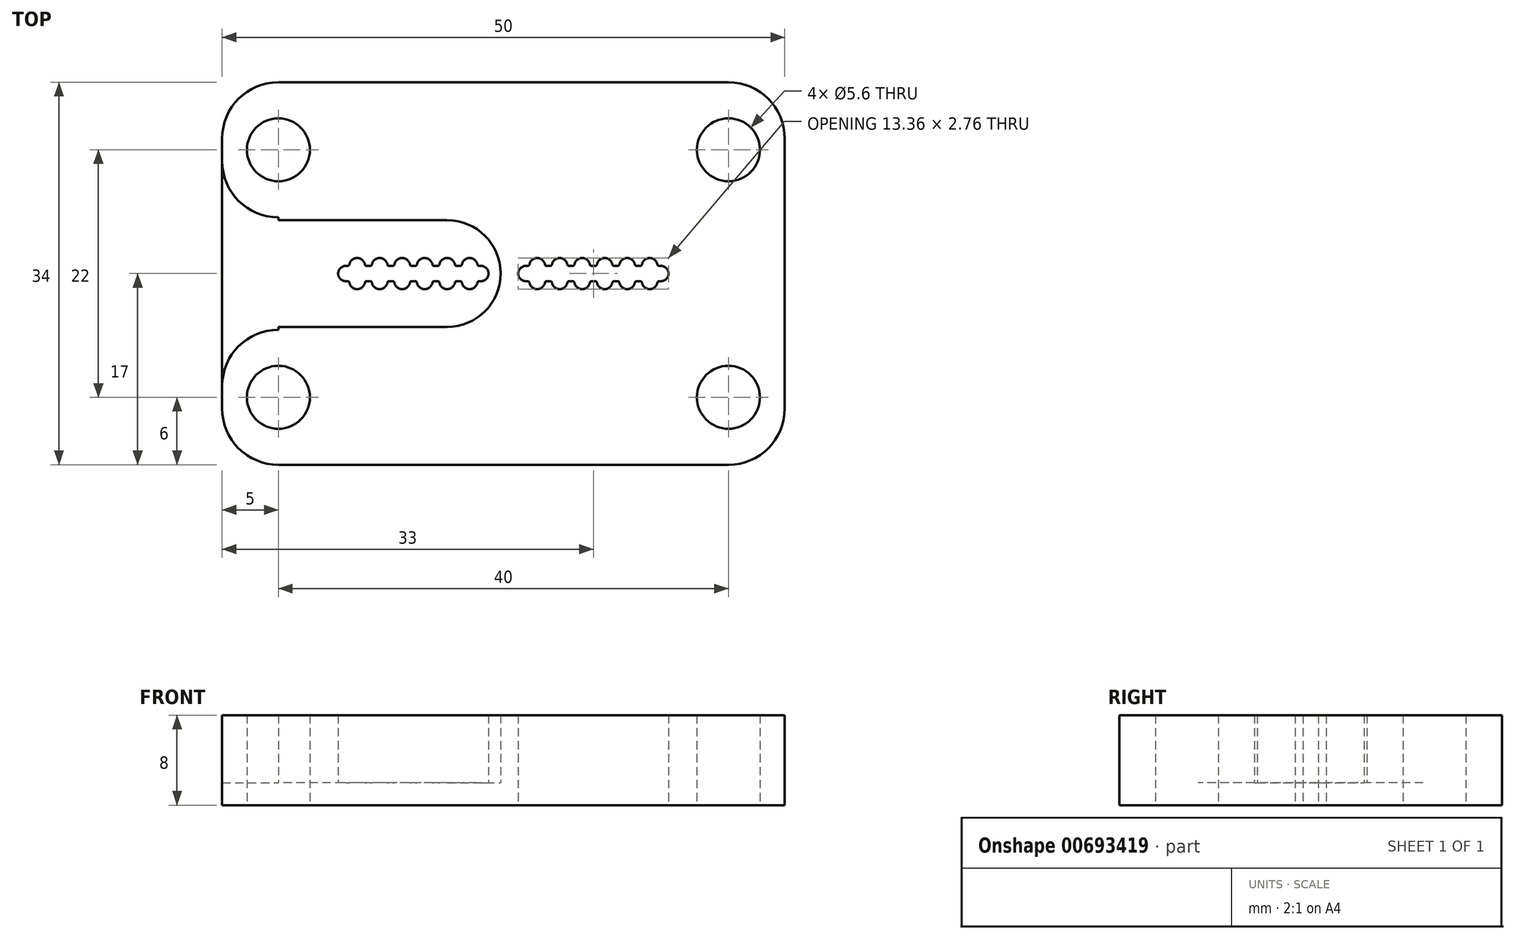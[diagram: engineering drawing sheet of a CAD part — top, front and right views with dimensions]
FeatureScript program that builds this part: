
annotation { "Feature Type Name" : "Feature", "Feature Type Description" : "" }
export const myFeature = defineFeature(function(context is Context, id is Id, definition is map)
    precondition{}
    {
        {
            var Q0;
            Q0=qCreatedBy(makeId("Top.planeOp"),FACE);
            var sketch = newSketch(context, id + "F0", { "sketchPlane" : qUnion([Q0])});
            skLineSegment(sketch, "E0.bottom", {"start": v(-25, 17) * mm, "end": v(25, 17) * mm, "construction": true});
            skLineSegment(sketch, "E0.top", {"start": v(-25, -17) * mm, "end": v(25, -17) * mm, "construction": true});
            skLineSegment(sketch, "E0.left", {"start": v(-25, -10) * mm, "end": v(-25, -12) * mm, "construction": true});
            skLineSegment(sketch, "E0.right", {"start": v(25, 17) * mm, "end": v(25, -17) * mm, "construction": true});
            skPoint(sketch, "E0.middle", {"position": v(0, 0) * mm});
            skLineSegment(sketch, "E1", {"start": v(25, 0) * mm, "end": v(-5, 0) * mm, "construction": true});
            skLineSegment(sketch, "E2", {"start": v(-4, 0) * mm, "end": v(-2, 0) * mm});
            skLineSegment(sketch, "E3", {"start": v(-2, 0.68) * mm, "end": v(-2.16, 0.68) * mm});
            skArc(sketch, "E4", {"start": v(-2.31, 0.8) * mm, "mid": v(-3, 1.38) * mm, "end": v(-3.69, 0.8) * mm});
            skArc(sketch, "E5.filletArc", {"start": v(-2.31, 0.8) * mm, "mid": v(-2.26, 0.71) * mm, "end": v(-2.16, 0.68) * mm});
            skLineSegment(sketch, "E6", {"start": v(-4, 0.68) * mm, "end": v(-3.84, 0.68) * mm});
            skPoint(sketch, "E7.visualSharp", {"position": v(-3.7, 0.68) * mm});
            skArc(sketch, "E7.filletArc", {"start": v(-3.84, 0.68) * mm, "mid": v(-3.74, 0.71) * mm, "end": v(-3.69, 0.8) * mm});
            skLineSegment(sketch, "E8", {"start": v(0, -17) * mm, "end": v(0, 17) * mm, "construction": true});
            skLineSegment(sketch, "E9.1.0.0", {"start": v(-6, 0.68) * mm, "end": v(-5.84, 0.68) * mm});
            skArc(sketch, "E9.1.0.1", {"start": v(-4.31, 0.8) * mm, "mid": v(-5, 1.38) * mm, "end": v(-5.69, 0.8) * mm});
            skArc(sketch, "E9.1.0.2", {"start": v(-5.84, 0.68) * mm, "mid": v(-5.74, 0.71) * mm, "end": v(-5.69, 0.8) * mm});
            skArc(sketch, "E9.1.0.3", {"start": v(-4.31, 0.8) * mm, "mid": v(-4.26, 0.71) * mm, "end": v(-4.16, 0.68) * mm});
            skLineSegment(sketch, "E9.1.0.4", {"start": v(-4, 0.68) * mm, "end": v(-4.16, 0.68) * mm});
            skLineSegment(sketch, "E9.2.0.0", {"start": v(-8, 0.68) * mm, "end": v(-7.84, 0.68) * mm});
            skArc(sketch, "E9.2.0.1", {"start": v(-6.31, 0.8) * mm, "mid": v(-7, 1.38) * mm, "end": v(-7.69, 0.8) * mm});
            skArc(sketch, "E9.2.0.2", {"start": v(-7.84, 0.68) * mm, "mid": v(-7.74, 0.71) * mm, "end": v(-7.69, 0.8) * mm});
            skArc(sketch, "E9.2.0.3", {"start": v(-6.31, 0.8) * mm, "mid": v(-6.26, 0.71) * mm, "end": v(-6.16, 0.68) * mm});
            skLineSegment(sketch, "E9.2.0.4", {"start": v(-6, 0.68) * mm, "end": v(-6.16, 0.68) * mm});
            skLineSegment(sketch, "E9.3.0.0", {"start": v(-10, 0.68) * mm, "end": v(-9.84, 0.68) * mm});
            skArc(sketch, "E9.3.0.1", {"start": v(-8.31, 0.8) * mm, "mid": v(-9, 1.38) * mm, "end": v(-9.69, 0.8) * mm});
            skArc(sketch, "E9.3.0.2", {"start": v(-9.84, 0.68) * mm, "mid": v(-9.74, 0.71) * mm, "end": v(-9.69, 0.8) * mm});
            skArc(sketch, "E9.3.0.3", {"start": v(-8.31, 0.8) * mm, "mid": v(-8.26, 0.71) * mm, "end": v(-8.16, 0.68) * mm});
            skLineSegment(sketch, "E9.3.0.4", {"start": v(-8, 0.68) * mm, "end": v(-8.16, 0.68) * mm});
            skLineSegment(sketch, "E9.4.0.0", {"start": v(-12, 0.68) * mm, "end": v(-11.84, 0.68) * mm});
            skArc(sketch, "E9.4.0.1", {"start": v(-10.31, 0.8) * mm, "mid": v(-11, 1.38) * mm, "end": v(-11.69, 0.8) * mm});
            skArc(sketch, "E9.4.0.2", {"start": v(-11.84, 0.68) * mm, "mid": v(-11.74, 0.71) * mm, "end": v(-11.69, 0.8) * mm});
            skArc(sketch, "E9.4.0.3", {"start": v(-10.31, 0.8) * mm, "mid": v(-10.26, 0.71) * mm, "end": v(-10.16, 0.68) * mm});
            skLineSegment(sketch, "E9.4.0.4", {"start": v(-10, 0.68) * mm, "end": v(-10.16, 0.68) * mm});
            skLineSegment(sketch, "E9.5.0.0", {"start": v(-14, 0.68) * mm, "end": v(-13.84, 0.68) * mm});
            skArc(sketch, "E9.5.0.1", {"start": v(-12.31, 0.8) * mm, "mid": v(-13, 1.38) * mm, "end": v(-13.69, 0.8) * mm});
            skArc(sketch, "E9.5.0.2", {"start": v(-13.84, 0.68) * mm, "mid": v(-13.74, 0.71) * mm, "end": v(-13.69, 0.8) * mm});
            skArc(sketch, "E9.5.0.3", {"start": v(-12.31, 0.8) * mm, "mid": v(-12.26, 0.71) * mm, "end": v(-12.16, 0.68) * mm});
            skLineSegment(sketch, "E9.5.0.4", {"start": v(-12, 0.68) * mm, "end": v(-12.16, 0.68) * mm});
            skLineSegment(sketch, "E9.direction1", {"start": v(-4, 0.68) * mm, "end": v(-6, 0.68) * mm, "construction": true});
            skLineSegment(sketch, "E10", {"start": v(-14, 0.68) * mm, "end": v(-14, 0) * mm});
            skLineSegment(sketch, "E11", {"start": v(-5, 0) * mm, "end": v(-4, 0) * mm});
            skLineSegment(sketch, "E12.MirrorCS", {"start": v(-14, -0.68) * mm, "end": v(-13.84, -0.68) * mm});
            skArc(sketch, "E13.MirrorCS", {"start": v(-13.84, -0.68) * mm, "mid": v(-13.74, -0.71) * mm, "end": v(-13.69, -0.8) * mm});
            skArc(sketch, "E14.MirrorCS", {"start": v(-12.31, -0.8) * mm, "mid": v(-13, -1.38) * mm, "end": v(-13.69, -0.8) * mm});
            skArc(sketch, "E15.MirrorCS", {"start": v(-12.31, -0.8) * mm, "mid": v(-12.26, -0.71) * mm, "end": v(-12.16, -0.68) * mm});
            skLineSegment(sketch, "E16.MirrorCS", {"start": v(-12, -0.68) * mm, "end": v(-12.16, -0.68) * mm});
            skLineSegment(sketch, "E17.MirrorCS", {"start": v(-12, -0.68) * mm, "end": v(-11.84, -0.68) * mm});
            skArc(sketch, "E18.MirrorCS", {"start": v(-11.84, -0.68) * mm, "mid": v(-11.74, -0.71) * mm, "end": v(-11.69, -0.8) * mm});
            skArc(sketch, "E19.MirrorCS", {"start": v(-10.31, -0.8) * mm, "mid": v(-11, -1.38) * mm, "end": v(-11.69, -0.8) * mm});
            skArc(sketch, "E20.MirrorCS", {"start": v(-10.31, -0.8) * mm, "mid": v(-10.26, -0.71) * mm, "end": v(-10.16, -0.68) * mm});
            skLineSegment(sketch, "E21.MirrorCS", {"start": v(-10, -0.68) * mm, "end": v(-9.84, -0.68) * mm});
            skArc(sketch, "E22.MirrorCS", {"start": v(-9.84, -0.68) * mm, "mid": v(-9.74, -0.71) * mm, "end": v(-9.69, -0.8) * mm});
            skLineSegment(sketch, "E23.MirrorCS", {"start": v(-10, -0.68) * mm, "end": v(-10.16, -0.68) * mm});
            skArc(sketch, "E24.MirrorCS", {"start": v(-8.31, -0.8) * mm, "mid": v(-9, -1.38) * mm, "end": v(-9.69, -0.8) * mm});
            skArc(sketch, "E25.MirrorCS", {"start": v(-8.31, -0.8) * mm, "mid": v(-8.26, -0.71) * mm, "end": v(-8.16, -0.68) * mm});
            skArc(sketch, "E26.MirrorCS", {"start": v(-7.84, -0.68) * mm, "mid": v(-7.74, -0.71) * mm, "end": v(-7.69, -0.8) * mm});
            skLineSegment(sketch, "E27.MirrorCS", {"start": v(25, -17) * mm, "end": v(25, 17) * mm, "construction": true});
            skArc(sketch, "E28.MirrorCS", {"start": v(-6.31, -0.8) * mm, "mid": v(-7, -1.38) * mm, "end": v(-7.69, -0.8) * mm});
            skArc(sketch, "E29.MirrorCS", {"start": v(-6.31, -0.8) * mm, "mid": v(-6.26, -0.71) * mm, "end": v(-6.16, -0.68) * mm});
            skArc(sketch, "E30.MirrorCS", {"start": v(-5.84, -0.68) * mm, "mid": v(-5.74, -0.71) * mm, "end": v(-5.69, -0.8) * mm});
            skArc(sketch, "E31.MirrorCS", {"start": v(-4.31, -0.8) * mm, "mid": v(-5, -1.38) * mm, "end": v(-5.69, -0.8) * mm});
            skArc(sketch, "E32.MirrorCS", {"start": v(-4.31, -0.8) * mm, "mid": v(-4.26, -0.71) * mm, "end": v(-4.16, -0.68) * mm});
            skArc(sketch, "E33.MirrorCS", {"start": v(-3.84, -0.68) * mm, "mid": v(-3.74, -0.71) * mm, "end": v(-3.69, -0.8) * mm});
            skLineSegment(sketch, "E34.MirrorCS", {"start": v(-2, -0.68) * mm, "end": v(-2.16, -0.68) * mm});
            skArc(sketch, "E35.MirrorCS", {"start": v(-2.31, -0.8) * mm, "mid": v(-3, -1.38) * mm, "end": v(-3.69, -0.8) * mm});
            skArc(sketch, "E36.MirrorCS", {"start": v(-2.31, -0.8) * mm, "mid": v(-2.26, -0.71) * mm, "end": v(-2.16, -0.68) * mm});
            skLineSegment(sketch, "E37", {"start": v(-8.16, -0.68) * mm, "end": v(-7.84, -0.68) * mm});
            skLineSegment(sketch, "E38", {"start": v(-6.16, -0.68) * mm, "end": v(-5.84, -0.68) * mm});
            skLineSegment(sketch, "E39", {"start": v(-4.16, -0.68) * mm, "end": v(-3.84, -0.68) * mm});
            skArc(sketch, "E40", {"start": v(-2, -0.68) * mm, "mid": v(-1.32, 0) * mm, "end": v(-2, 0.68) * mm});
            skLineSegment(sketch, "E41.bottom", {"start": v(-20, -5) * mm, "end": v(-5, -5) * mm, "construction": true});
            skLineSegment(sketch, "E41.top", {"start": v(-20, 5) * mm, "end": v(-5, 5) * mm, "construction": true});
            skArc(sketch, "E42", {"start": v(-5, -5) * mm, "mid": v(0, 0) * mm, "end": v(-5, 5) * mm, "construction": true});
            skLineSegment(sketch, "E43", {"start": v(-25, 10) * mm, "end": v(-25, 12) * mm});
            skLineSegment(sketch, "E44", {"start": v(-20, 17) * mm, "end": v(0, 17) * mm});
            skLineSegment(sketch, "E45", {"start": v(-20, -17) * mm, "end": v(0, -17) * mm});
            skPoint(sketch, "E46.visualSharp", {"position": v(-25, 5) * mm});
            skArc(sketch, "E46.filletArc", {"start": v(-25, 10) * mm, "mid": v(-23.54, 6.46) * mm, "end": v(-20, 5) * mm});
            skPoint(sketch, "E47.visualSharp", {"position": v(-25, 17) * mm});
            skArc(sketch, "E47.filletArc", {"start": v(-20, 17) * mm, "mid": v(-23.54, 15.54) * mm, "end": v(-25, 12) * mm});
            skPoint(sketch, "E48.visualSharp", {"position": v(-25, -17) * mm});
            skArc(sketch, "E48.filletArc", {"start": v(-25, -12) * mm, "mid": v(-23.54, -15.54) * mm, "end": v(-20, -17) * mm});
            skPoint(sketch, "E49.newPointB", {"position": v(-25, -5) * mm});
            skArc(sketch, "E49.filletArc", {"start": v(-20, -5) * mm, "mid": v(-23.54, -6.46) * mm, "end": v(-25, -10) * mm});
            skLineSegment(sketch, "E50", {"start": v(-20, -10) * mm, "end": v(-20, -12) * mm, "construction": true});
            skCircle(sketch, "E51", {"center": v(-20, -11) * mm, "radius": 2.8 * mm});
            skCircle(sketch, "E52.MirrorC", {"center": v(-20, 11) * mm, "radius": 2.8 * mm});
            skLineSegment(sketch, "E53", {"start": v(-25, 10) * mm, "end": v(-25, -10) * mm});
            skArc(sketch, "E54.MirrorCS", {"start": v(5, -5) * mm, "mid": v(0, 0) * mm, "end": v(5, 5) * mm, "construction": true});
            skLineSegment(sketch, "E55.MirrorCS", {"start": v(20, -5) * mm, "end": v(5, -5) * mm, "construction": true});
            skLineSegment(sketch, "E56.MirrorCS", {"start": v(20, 5) * mm, "end": v(5, 5) * mm, "construction": true});
            skArc(sketch, "E57.MirrorCS", {"start": v(20, -5) * mm, "mid": v(23.54, -6.46) * mm, "end": v(25, -10) * mm});
            skArc(sketch, "E58.MirrorCS", {"start": v(25, -12) * mm, "mid": v(23.54, -15.54) * mm, "end": v(20, -17) * mm});
            skCircle(sketch, "E59.MirrorC", {"center": v(20, -11) * mm, "radius": 2.8 * mm});
            skLineSegment(sketch, "E60.MirrorCS", {"start": v(20, -17) * mm, "end": v(0, -17) * mm});
            skLineSegment(sketch, "E61.MirrorCS", {"start": v(25, 10) * mm, "end": v(25, -10) * mm});
            skArc(sketch, "E62.MirrorCS", {"start": v(25, 10) * mm, "mid": v(23.54, 6.46) * mm, "end": v(20, 5) * mm});
            skCircle(sketch, "E63.MirrorC", {"center": v(20, 11) * mm, "radius": 2.8 * mm});
            skArc(sketch, "E64.MirrorCS", {"start": v(20, 17) * mm, "mid": v(23.54, 15.54) * mm, "end": v(25, 12) * mm});
            skLineSegment(sketch, "E65.MirrorCS", {"start": v(20, 17) * mm, "end": v(0, 17) * mm});
            skArc(sketch, "E66.MirrorCS", {"start": v(2, -0.68) * mm, "mid": v(1.32, 0) * mm, "end": v(2, 0.68) * mm});
            skArc(sketch, "E67.MirrorCS", {"start": v(2.31, -0.8) * mm, "mid": v(3, -1.38) * mm, "end": v(3.69, -0.8) * mm});
            skArc(sketch, "E68.MirrorCS", {"start": v(2.31, -0.8) * mm, "mid": v(2.26, -0.71) * mm, "end": v(2.16, -0.68) * mm});
            skArc(sketch, "E69.MirrorCS", {"start": v(2.31, 0.8) * mm, "mid": v(2.26, 0.71) * mm, "end": v(2.16, 0.68) * mm});
            skArc(sketch, "E70.MirrorCS", {"start": v(2.31, 0.8) * mm, "mid": v(3, 1.38) * mm, "end": v(3.69, 0.8) * mm});
            skArc(sketch, "E71.MirrorCS", {"start": v(3.84, 0.68) * mm, "mid": v(3.74, 0.71) * mm, "end": v(3.69, 0.8) * mm});
            skLineSegment(sketch, "E72.MirrorCS", {"start": v(4, 0.68) * mm, "end": v(3.84, 0.68) * mm});
            skLineSegment(sketch, "E73.MirrorCS", {"start": v(4, 0.68) * mm, "end": v(4.16, 0.68) * mm});
            skArc(sketch, "E74.MirrorCS", {"start": v(4.31, 0.8) * mm, "mid": v(4.26, 0.71) * mm, "end": v(4.16, 0.68) * mm});
            skArc(sketch, "E75.MirrorCS", {"start": v(4.31, 0.8) * mm, "mid": v(5, 1.38) * mm, "end": v(5.69, 0.8) * mm});
            skArc(sketch, "E76.MirrorCS", {"start": v(5.84, 0.68) * mm, "mid": v(5.74, 0.71) * mm, "end": v(5.69, 0.8) * mm});
            skArc(sketch, "E77.MirrorCS", {"start": v(12.31, -0.8) * mm, "mid": v(12.26, -0.71) * mm, "end": v(12.16, -0.68) * mm});
            skLineSegment(sketch, "E78.MirrorCS", {"start": v(6, 0.68) * mm, "end": v(6.16, 0.68) * mm});
            skLineSegment(sketch, "E79.MirrorCS", {"start": v(6, 0.68) * mm, "end": v(5.84, 0.68) * mm});
            skArc(sketch, "E80.MirrorCS", {"start": v(6.31, 0.8) * mm, "mid": v(6.26, 0.71) * mm, "end": v(6.16, 0.68) * mm});
            skArc(sketch, "E81.MirrorCS", {"start": v(6.31, 0.8) * mm, "mid": v(7, 1.38) * mm, "end": v(7.69, 0.8) * mm});
            skArc(sketch, "E82.MirrorCS", {"start": v(7.84, 0.68) * mm, "mid": v(7.74, 0.71) * mm, "end": v(7.69, 0.8) * mm});
            skLineSegment(sketch, "E83.MirrorCS", {"start": v(8, 0.68) * mm, "end": v(7.84, 0.68) * mm});
            skLineSegment(sketch, "E84.MirrorCS", {"start": v(2, -0.68) * mm, "end": v(2.16, -0.68) * mm});
            skLineSegment(sketch, "E85.MirrorCS", {"start": v(8, 0.68) * mm, "end": v(8.16, 0.68) * mm});
            skArc(sketch, "E86.MirrorCS", {"start": v(8.31, 0.8) * mm, "mid": v(8.26, 0.71) * mm, "end": v(8.16, 0.68) * mm});
            skLineSegment(sketch, "E87.MirrorCS", {"start": v(10, 0.68) * mm, "end": v(9.84, 0.68) * mm});
            skArc(sketch, "E88.MirrorCS", {"start": v(8.31, 0.8) * mm, "mid": v(9, 1.38) * mm, "end": v(9.69, 0.8) * mm});
            skArc(sketch, "E89.MirrorCS", {"start": v(9.84, 0.68) * mm, "mid": v(9.74, 0.71) * mm, "end": v(9.69, 0.8) * mm});
            skLineSegment(sketch, "E90.MirrorCS", {"start": v(10, 0.68) * mm, "end": v(10.16, 0.68) * mm});
            skArc(sketch, "E91.MirrorCS", {"start": v(10.31, 0.8) * mm, "mid": v(10.26, 0.71) * mm, "end": v(10.16, 0.68) * mm});
            skArc(sketch, "E92.MirrorCS", {"start": v(10.31, 0.8) * mm, "mid": v(11, 1.38) * mm, "end": v(11.69, 0.8) * mm});
            skArc(sketch, "E93.MirrorCS", {"start": v(11.84, 0.68) * mm, "mid": v(11.74, 0.71) * mm, "end": v(11.69, 0.8) * mm});
            skLineSegment(sketch, "E94.MirrorCS", {"start": v(12, 0.68) * mm, "end": v(11.84, 0.68) * mm});
            skLineSegment(sketch, "E95.MirrorCS", {"start": v(12, 0.68) * mm, "end": v(12.16, 0.68) * mm});
            skArc(sketch, "E96.MirrorCS", {"start": v(12.31, 0.8) * mm, "mid": v(12.26, 0.71) * mm, "end": v(12.16, 0.68) * mm});
            skArc(sketch, "E97.MirrorCS", {"start": v(12.31, 0.8) * mm, "mid": v(13, 1.38) * mm, "end": v(13.69, 0.8) * mm});
            skArc(sketch, "E98.MirrorCS", {"start": v(13.84, 0.68) * mm, "mid": v(13.74, 0.71) * mm, "end": v(13.69, 0.8) * mm});
            skLineSegment(sketch, "E99.MirrorCS", {"start": v(14, 0.68) * mm, "end": v(13.84, 0.68) * mm});
            skLineSegment(sketch, "E100.MirrorCS", {"start": v(14, -0.68) * mm, "end": v(13.84, -0.68) * mm});
            skArc(sketch, "E101.MirrorCS", {"start": v(13.84, -0.68) * mm, "mid": v(13.74, -0.71) * mm, "end": v(13.69, -0.8) * mm});
            skLineSegment(sketch, "E102.MirrorCS", {"start": v(2, 0.68) * mm, "end": v(2.16, 0.68) * mm});
            skArc(sketch, "E103.MirrorCS", {"start": v(12.31, -0.8) * mm, "mid": v(13, -1.38) * mm, "end": v(13.69, -0.8) * mm});
            skLineSegment(sketch, "E104.MirrorCS", {"start": v(12, -0.68) * mm, "end": v(12.16, -0.68) * mm});
            skLineSegment(sketch, "E105.MirrorCS", {"start": v(12, -0.68) * mm, "end": v(11.84, -0.68) * mm});
            skArc(sketch, "E106.MirrorCS", {"start": v(11.84, -0.68) * mm, "mid": v(11.74, -0.71) * mm, "end": v(11.69, -0.8) * mm});
            skArc(sketch, "E107.MirrorCS", {"start": v(10.31, -0.8) * mm, "mid": v(11, -1.38) * mm, "end": v(11.69, -0.8) * mm});
            skArc(sketch, "E108.MirrorCS", {"start": v(10.31, -0.8) * mm, "mid": v(10.26, -0.71) * mm, "end": v(10.16, -0.68) * mm});
            skLineSegment(sketch, "E109.MirrorCS", {"start": v(10, -0.68) * mm, "end": v(10.16, -0.68) * mm});
            skLineSegment(sketch, "E110.MirrorCS", {"start": v(10, -0.68) * mm, "end": v(9.84, -0.68) * mm});
            skArc(sketch, "E111.MirrorCS", {"start": v(9.84, -0.68) * mm, "mid": v(9.74, -0.71) * mm, "end": v(9.69, -0.8) * mm});
            skArc(sketch, "E112.MirrorCS", {"start": v(8.31, -0.8) * mm, "mid": v(9, -1.38) * mm, "end": v(9.69, -0.8) * mm});
            skArc(sketch, "E113.MirrorCS", {"start": v(8.31, -0.8) * mm, "mid": v(8.26, -0.71) * mm, "end": v(8.16, -0.68) * mm});
            skLineSegment(sketch, "E114.MirrorCS", {"start": v(8.16, -0.68) * mm, "end": v(7.84, -0.68) * mm});
            skArc(sketch, "E115.MirrorCS", {"start": v(7.84, -0.68) * mm, "mid": v(7.74, -0.71) * mm, "end": v(7.69, -0.8) * mm});
            skArc(sketch, "E116.MirrorCS", {"start": v(6.31, -0.8) * mm, "mid": v(7, -1.38) * mm, "end": v(7.69, -0.8) * mm});
            skArc(sketch, "E117.MirrorCS", {"start": v(6.31, -0.8) * mm, "mid": v(6.26, -0.71) * mm, "end": v(6.16, -0.68) * mm});
            skLineSegment(sketch, "E118.MirrorCS", {"start": v(6.16, -0.68) * mm, "end": v(5.84, -0.68) * mm});
            skArc(sketch, "E119.MirrorCS", {"start": v(5.84, -0.68) * mm, "mid": v(5.74, -0.71) * mm, "end": v(5.69, -0.8) * mm});
            skArc(sketch, "E120.MirrorCS", {"start": v(4.31, -0.8) * mm, "mid": v(5, -1.38) * mm, "end": v(5.69, -0.8) * mm});
            skArc(sketch, "E121.MirrorCS", {"start": v(4.31, -0.8) * mm, "mid": v(4.26, -0.71) * mm, "end": v(4.16, -0.68) * mm});
            skLineSegment(sketch, "E122.MirrorCS", {"start": v(4.16, -0.68) * mm, "end": v(3.84, -0.68) * mm});
            skLineSegment(sketch, "E123.MirrorCS", {"start": v(4, 0.68) * mm, "end": v(6, 0.68) * mm, "construction": true});
            skArc(sketch, "E124.MirrorCS", {"start": v(3.84, -0.68) * mm, "mid": v(3.74, -0.71) * mm, "end": v(3.69, -0.8) * mm});
            skArc(sketch, "E125", {"start": v(14, -0.68) * mm, "mid": v(14.68, 0) * mm, "end": v(14, 0.68) * mm});
            skLineSegment(sketch, "E126", {"start": v(25, 12) * mm, "end": v(25, 10) * mm});
            skLineSegment(sketch, "E127", {"start": v(25, -12) * mm, "end": v(25, -10) * mm});
            skLineSegment(sketch, "E128", {"start": v(-25, -12) * mm, "end": v(-25, -10) * mm});
            skArc(sketch, "E129", {"start": v(-14, 0.68) * mm, "mid": v(-14.68, 0) * mm, "end": v(-14, -0.68) * mm});
            skLineSegment(sketch, "E130.trimOffspring", {"start": v(-14, 0) * mm, "end": v(-25, 0) * mm, "construction": true});
            skPoint(sketch, "E131.MirrorCS.end.orphan", {"position": v(-2, -0.68) * mm});
            skLineSegment(sketch, "E132.0", {"start": v(-20, -4.75) * mm, "end": v(-5, -4.75) * mm});
            skArc(sketch, "E132.1", {"start": v(-5, -4.75) * mm, "mid": v(-0.25, 0) * mm, "end": v(-5, 4.75) * mm});
            skLineSegment(sketch, "E132.2", {"start": v(-20, 4.75) * mm, "end": v(-5, 4.75) * mm});
            skLineSegment(sketch, "E133.0", {"start": v(20, 4.75) * mm, "end": v(5, 4.75) * mm});
            skArc(sketch, "E133.1", {"start": v(5, -4.75) * mm, "mid": v(0.25, 0) * mm, "end": v(5, 4.75) * mm});
            skLineSegment(sketch, "E133.2", {"start": v(20, -4.75) * mm, "end": v(5, -4.75) * mm});
            skLineSegment(sketch, "E134", {"start": v(-20, -4.75) * mm, "end": v(-20, -5) * mm});
            skLineSegment(sketch, "E135", {"start": v(-20, 4.75) * mm, "end": v(-20, 5) * mm});
            skLineSegment(sketch, "E136", {"start": v(20, -5) * mm, "end": v(20, -4.75) * mm});
            skLineSegment(sketch, "E137", {"start": v(20, 4.75) * mm, "end": v(20, 5) * mm});
            skSolve(sketch);
        }
        {
            var Q0;
            Q0=makeQuery(id+"F0.imprint","IMPRINT",FACE,{"disambiguationData":[TD([[makeQuery(id+"F0.imprint","IMPRINT",EDGE,{"derivedFrom":sQuery(id+"F0.wireOp",EDGE,"E3")}),-1.0]])]});
            var Q1;
            Q1=makeQuery(id+"F0.imprint","IMPRINT",FACE,{"disambiguationData":[TD([[makeQuery(id+"F0.imprint","IMPRINT",EDGE,{"derivedFrom":sQuery(id+"F0.wireOp",EDGE,"E57.MirrorCS")}),1.0]])]});
            extrude(context, id + "F1", {"entities" : qUnion([Q0, Q1]), "depth" : 2 * mm, "offsetDistance" : 25 * mm});
        }
        {
            var Q0;
            Q0=makeQuery(id+"F0.imprint","IMPRINT",FACE,{"disambiguationData":[TD([[makeQuery(id+"F0.imprint","IMPRINT",EDGE,{"derivedFrom":sQuery(id+"F0.wireOp",EDGE,"E43")}),-1.0]])]});
            var Q1;
            Q1=makeQuery(id+"F0.imprint","IMPRINT",FACE,{"disambiguationData":[TD([[makeQuery(id+"F0.imprint","IMPRINT",EDGE,{"derivedFrom":sQuery(id+"F0.wireOp",EDGE,"E66.MirrorCS")}),-1.0]])]});
            var Q2;
            Q2=makeQuery(id+"F0.imprint","IMPRINT",FACE,{"disambiguationData":[TD([[makeQuery(id+"F0.imprint","IMPRINT",EDGE,{"derivedFrom":sQuery(id+"F0.wireOp",EDGE,"E3")}),1.0]])]});
            extrude(context, id + "F2", {"entities" : qUnion([Q0, Q1, Q2]), "operationType" : NewBodyOperationType.ADD, "depth" : 8 * mm, "offsetDistance" : 25 * mm});
        }
    });
